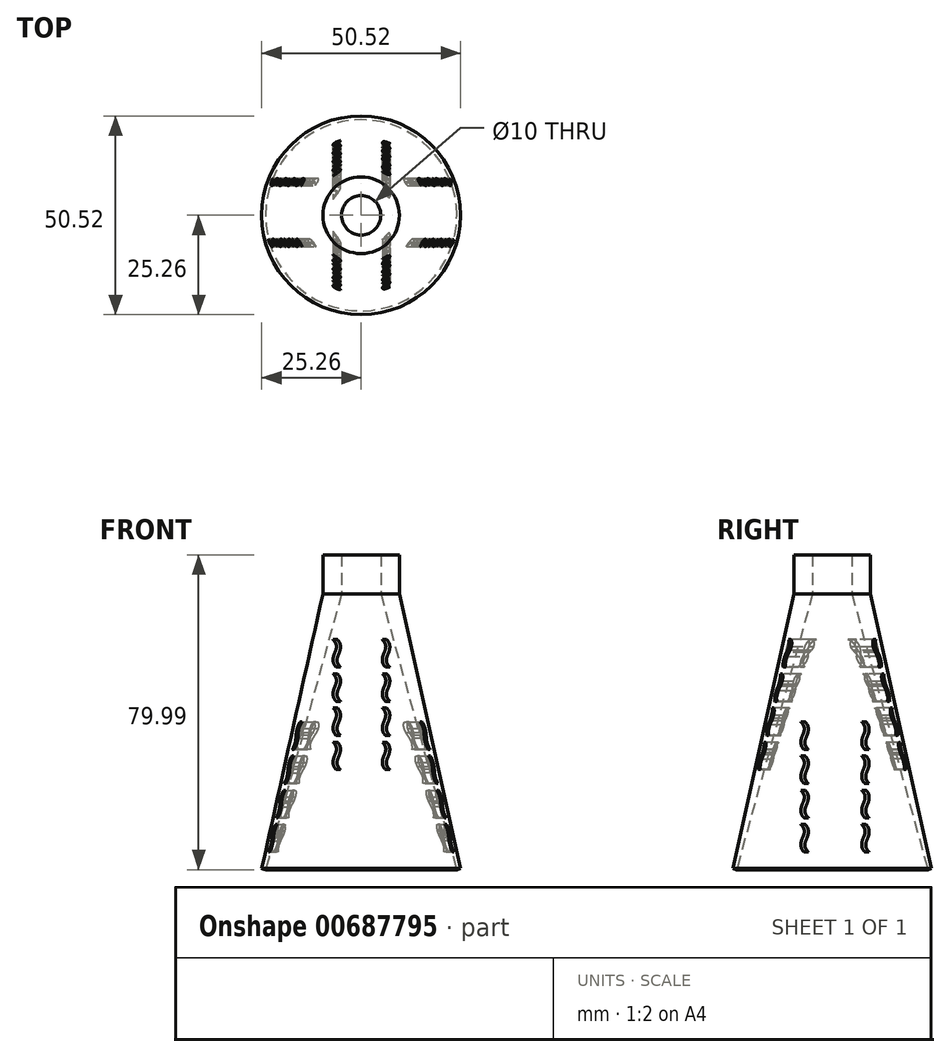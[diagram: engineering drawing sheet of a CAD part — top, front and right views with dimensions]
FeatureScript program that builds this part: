
annotation { "Feature Type Name" : "Feature", "Feature Type Description" : "" }
export const myFeature = defineFeature(function(context is Context, id is Id, definition is map)
    precondition{}
    {
        {
            var Q0;
            Q0=qCreatedBy(makeId("Front.planeOp"),FACE);
            var sketch = newSketch(context, id + "F0", { "sketchPlane" : qUnion([Q0])});
            skLineSegment(sketch, "E0", {"start": v(0, 0) * mm, "end": v(0, 70) * mm});
            skLineSegment(sketch, "E1", {"start": v(0, 70) * mm, "end": v(5, 70) * mm});
            skLineSegment(sketch, "E2", {"start": v(5, 70) * mm, "end": v(24.3, 0) * mm});
            skLineSegment(sketch, "E3", {"start": v(24.3, 0) * mm, "end": v(25.26, 0.27) * mm});
            skLineSegment(sketch, "E4", {"start": v(25.26, 0.27) * mm, "end": v(9.73, 70) * mm});
            skLineSegment(sketch, "E5", {"start": v(9.73, 70) * mm, "end": v(5, 70) * mm});
            skLineSegment(sketch, "E6", {"start": v(9.73, 70) * mm, "end": v(9.73, 79.99) * mm});
            skLineSegment(sketch, "E7", {"start": v(9.73, 79.99) * mm, "end": v(5, 79.99) * mm});
            skLineSegment(sketch, "E8", {"start": v(5, 79.99) * mm, "end": v(5, 70) * mm});
            skSolve(sketch);
        }
        {
            var Q0;
            Q0 = qSketchRegion(id + "F0", true);
            var Q1;
            Q1=sQuery(id+"F0.wireOp",EDGE,"E0");
            revolve(context, id + "F1", {"entities" : qUnion([Q0]), "axis" : qUnion([Q1]), "revolveType" : RevolveType.FULL});
        }
        {
            var Q0;
            Q0=qCreatedBy(makeId("Front.planeOp"),FACE);
            cPlane(context, id + "F2", {"entities" : qUnion([Q0]), "cplaneType" : CPlaneType.OFFSET, "offset" : 40 * mm, "width" : 150 * mm, "height" : 150 * mm});
        }
        {
            var Q0;
            Q0=qCreatedBy(id+"F2.planeOp",FACE);
            var sketch = newSketch(context, id + "F3", { "sketchPlane" : qUnion([Q0])});
            skText(sketch, "E9", { "text": "~", "fontName": "OpenSans-Regular.ttf"});
            skText(sketch, "E10", { "text": "~", "fontName": "OpenSans-Regular.ttf"});
            skText(sketch, "E11", { "text": "~", "fontName": "OpenSans-Regular.ttf"});
            skText(sketch, "E12", { "text": "~", "fontName": "OpenSans-Regular.ttf"});
            skText(sketch, "E13", { "text": "~", "fontName": "OpenSans-Regular.ttf"});
            skText(sketch, "E14", { "text": "~", "fontName": "OpenSans-Regular.ttf"});
            skText(sketch, "E15", { "text": "~", "fontName": "OpenSans-Regular.ttf"});
            skText(sketch, "E16", { "text": "~", "fontName": "OpenSans-Regular.ttf"});
            skText(sketch, "E17", { "text": "~", "fontName": "OpenSans-Regular.ttf"});
            skText(sketch, "E18", { "text": "~", "fontName": "OpenSans-Regular.ttf"});
            skText(sketch, "E19", { "text": "~", "fontName": "OpenSans-Regular.ttf"});
            skText(sketch, "E20", { "text": "~", "fontName": "OpenSans-Regular.ttf"});
            const initialGuessF3  = {"E9": [0.0011, 0.05052, 0, -1, 0.0107], "E10": [0.0011, 0.04182, 0, -1, 0.0107], "E11": [0.0011, 0.03313, 0, -1, 0.0107], "E12": [0.0011, 0.05918, 0, -1, 0.0107], "E13": [0.01306, 0.11218, 0, -1, 0.0107], "E14": [0.01306, 0.10348, 0, -1, 0.0107], "E15": [0.01306, 0.0948, 0, -1, 0.0107], "E16": [0.01306, 0.12084, 0, -1, 0.0107], "E17": [-0.01143, 0.05052, 0, -1, 0.0107], "E18": [-0.01143, 0.04183, 0, -1, 0.0107], "E19": [-0.01143, 0.03314, 0, -1, 0.0107], "E20": [-0.01143, 0.05918, 0, -1, 0.0107]};
            skSetInitialGuess(sketch, initialGuessF3);
            skSolve(sketch);
        }
        {
            var Q0;
            Q0 = qSketchRegion(id + "F3", true);
            extrude(context, id + "F4", {"entities" : qUnion([Q0]), "operationType" : NewBodyOperationType.REMOVE, "endBound" : BoundingType.THROUGH_ALL, "oppositeDirection" : true, "depth" : 25 * mm, "offsetDistance" : 25 * mm});
        }
        {
            var Q0;
            Q0=qCreatedBy(makeId("Right.planeOp"),FACE);
            cPlane(context, id + "F5", {"entities" : qUnion([Q0]), "cplaneType" : CPlaneType.OFFSET, "offset" : 25 * mm, "width" : 150 * mm, "height" : 150 * mm});
        }
        {
            var Q0;
            Q0=qCreatedBy(id+"F5.planeOp",FACE);
            var sketch = newSketch(context, id + "F6", { "sketchPlane" : qUnion([Q0])});
            skText(sketch, "E21", { "text": "~", "fontName": "OpenSans-Regular.ttf"});
            skText(sketch, "E22", { "text": "~", "fontName": "OpenSans-Regular.ttf"});
            skText(sketch, "E23", { "text": "~", "fontName": "OpenSans-Regular.ttf"});
            skText(sketch, "E24", { "text": "~", "fontName": "OpenSans-Regular.ttf"});
            skText(sketch, "E25", { "text": "~", "fontName": "OpenSans-Regular.ttf"});
            skText(sketch, "E26", { "text": "~", "fontName": "OpenSans-Regular.ttf"});
            skText(sketch, "E27", { "text": "~", "fontName": "OpenSans-Regular.ttf"});
            skText(sketch, "E28", { "text": "~", "fontName": "OpenSans-Regular.ttf"});
            const initialGuessF6  = {"E21": [-0.01225, 0.0296, 0, -1, 0.0107], "E22": [-0.01225, 0.02091, 0, -1, 0.0107], "E23": [-0.01225, 0.01222, 0, -1, 0.0107], "E24": [-0.01225, 0.03826, 0, -1, 0.0107], "E25": [0.0032, 0.0296, 0, -1, 0.0107], "E26": [0.0032, 0.02091, 0, -1, 0.0107], "E27": [0.0032, 0.01222, 0, -1, 0.0107], "E28": [0.0032, 0.03826, 0, -1, 0.0107]};
            skSetInitialGuess(sketch, initialGuessF6);
            skSolve(sketch);
        }
        {
            var Q0;
            Q0 = qSketchRegion(id + "F6", true);
            extrude(context, id + "F7", {"entities" : qUnion([Q0]), "operationType" : NewBodyOperationType.REMOVE, "endBound" : BoundingType.THROUGH_ALL, "oppositeDirection" : true, "depth" : 25 * mm, "offsetDistance" : 25 * mm});
        }
    });
